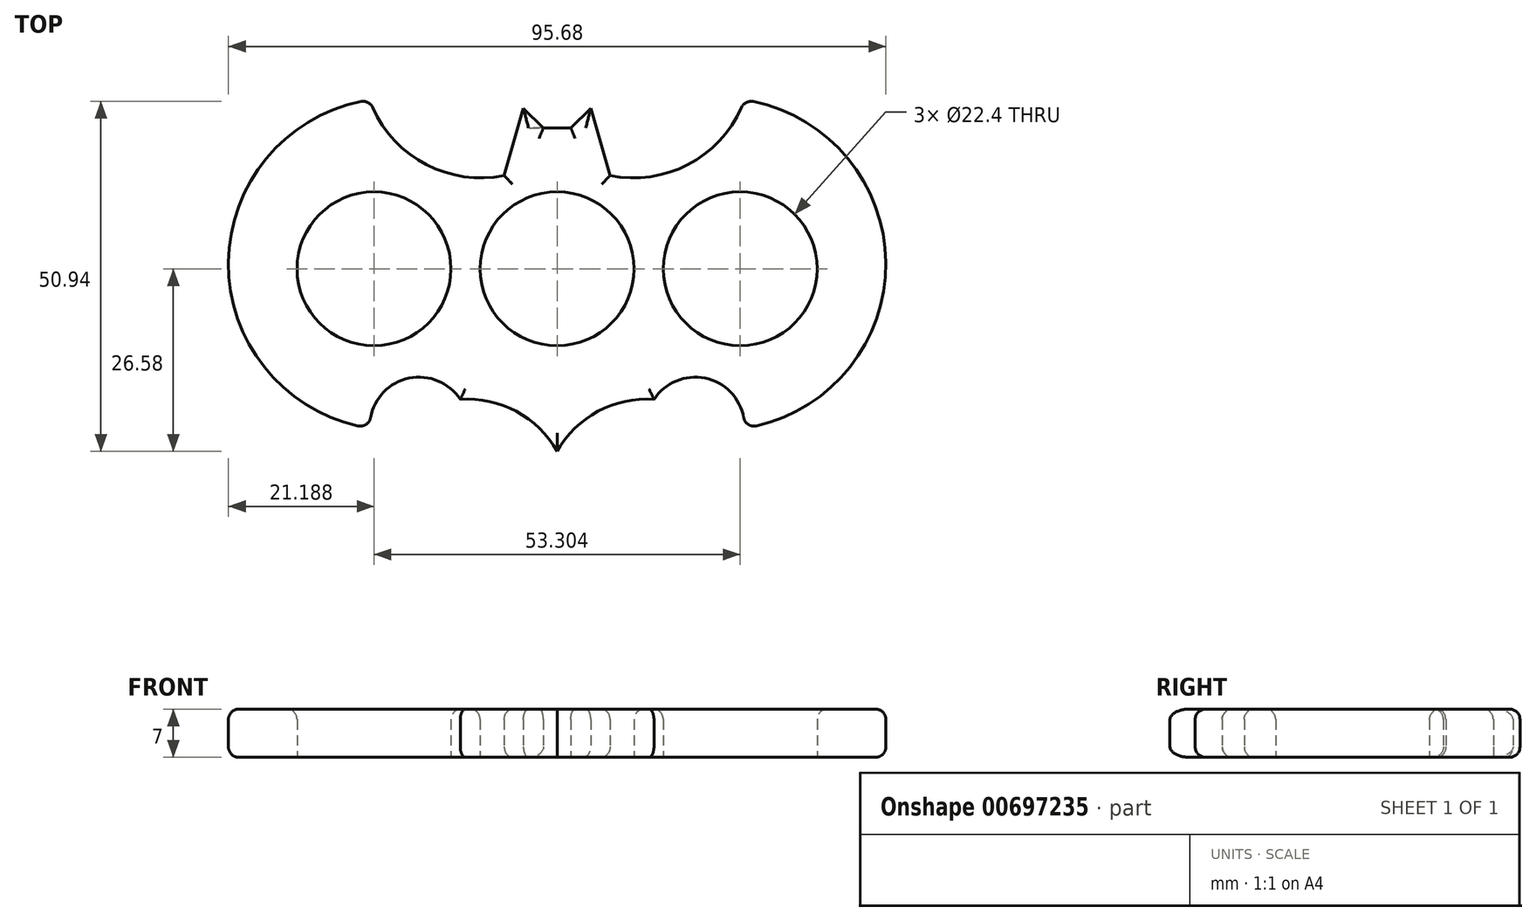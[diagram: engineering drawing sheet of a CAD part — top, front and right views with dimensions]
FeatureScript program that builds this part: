
annotation { "Feature Type Name" : "Feature", "Feature Type Description" : "" }
export const myFeature = defineFeature(function(context is Context, id is Id, definition is map)
    precondition{}
    {
        {
            var Q0;
            Q0=qCreatedBy(makeId("Top.planeOp"),FACE);
            var sketch = newSketch(context, id + "F0", { "sketchPlane" : qUnion([Q0])});
            skCircle(sketch, "E0", {"center": v(0, 0) * mm, "radius": 11.2 * mm});
            skCircle(sketch, "E1", {"center": v(26.65, 0) * mm, "radius": 11.2 * mm});
            skCircle(sketch, "E2.1.1", {"center": v(-26.65, 0) * mm, "radius": 11.2 * mm});
            skPoint(sketch, "E3.MirrorCS.end.orphan", {"position": v(7.9, 16.16) * mm});
            skPoint(sketch, "E4.end.orphan", {"position": v(-7.9, 16.16) * mm});
            skLineSegment(sketch, "E5", {"start": v(-7.7, 13.57) * mm, "end": v(-4.9, 23.35) * mm});
            skLineSegment(sketch, "E6", {"start": v(-4.9, 23.35) * mm, "end": v(-2, 20.49) * mm});
            skLineSegment(sketch, "E7.MirrorCS", {"start": v(7.7, 13.57) * mm, "end": v(4.9, 23.35) * mm});
            skLineSegment(sketch, "E8.MirrorCS", {"start": v(4.9, 23.35) * mm, "end": v(2, 20.49) * mm});
            skArc(sketch, "E9", {"start": v(-27.28, 24.55) * mm, "mid": v(-47.84, 0.68) * mm, "end": v(-27.28, -23.19) * mm});
            skPoint(sketch, "E10.MirrorCS.end.orphan", {"position": v(7.7, 13.57) * mm});
            skArc(sketch, "E11", {"start": v(-27.28, 24.55) * mm, "mid": v(-19.53, 15.43) * mm, "end": v(-7.7, 13.57) * mm});
            skLineSegment(sketch, "E12", {"start": v(-2, 20.49) * mm, "end": v(2, 20.49) * mm});
            skArc(sketch, "E13", {"start": v(-14.1, -19) * mm, "mid": v(-22.27, -16.11) * mm, "end": v(-27.28, -23.19) * mm});
            skArc(sketch, "E14", {"start": v(0, -26.58) * mm, "mid": v(-5.95, -20.75) * mm, "end": v(-14.1, -19) * mm});
            skArc(sketch, "E15.MirrorCS", {"start": v(27.28, 24.55) * mm, "mid": v(19.53, 15.43) * mm, "end": v(7.7, 13.57) * mm});
            skArc(sketch, "E16.MirrorCS", {"start": v(27.28, 24.55) * mm, "mid": v(47.84, 0.68) * mm, "end": v(27.28, -23.19) * mm});
            skArc(sketch, "E17.MirrorCS", {"start": v(14.1, -19) * mm, "mid": v(22.27, -16.11) * mm, "end": v(27.28, -23.19) * mm});
            skArc(sketch, "E18.MirrorCS", {"start": v(0, -26.58) * mm, "mid": v(5.95, -20.75) * mm, "end": v(14.1, -19) * mm});
            skSolve(sketch);
        }
        {
            var Q0;
            Q0=makeQuery(id+"F0.imprint","IMPRINT",FACE,{"disambiguationData":[TD([[makeQuery(id+"F0.imprint","IMPRINT",EDGE,{"derivedFrom":sQuery(id+"F0.wireOp",EDGE,"E0")}),-1.0]])]});
            extrude(context, id + "F1", {"entities" : qUnion([Q0]), "depth" : 7 * mm, "offsetDistance" : 25 * mm});
        }
        {
            var Q0;
            Q0=makeQuery(id+"F1.opExtrude","CAP_FACE",FACE,{"disambiguationData":[OSD([sQuery(id+"F0.wireOp",EDGE,"E0"),sQuery(id+"F0.wireOp",EDGE,"E1"),sQuery(id+"F0.wireOp",EDGE,"E2.1.1"),sQuery(id+"F0.wireOp",EDGE,"E5"),sQuery(id+"F0.wireOp",EDGE,"E6"),sQuery(id+"F0.wireOp",EDGE,"E8.MirrorCS"),sQuery(id+"F0.wireOp",EDGE,"E9"),sQuery(id+"F0.wireOp",EDGE,"E11"),sQuery(id+"F0.wireOp",EDGE,"E12"),sQuery(id+"F0.wireOp",EDGE,"E13"),sQuery(id+"F0.wireOp",EDGE,"E14"),sQuery(id+"F0.wireOp",EDGE,"E7.MirrorCS"),sQuery(id+"F0.wireOp",EDGE,"E15.MirrorCS"),sQuery(id+"F0.wireOp",EDGE,"E16.MirrorCS"),sQuery(id+"F0.wireOp",EDGE,"E17.MirrorCS"),sQuery(id+"F0.wireOp",EDGE,"E18.MirrorCS")])],"isStart":false});
            var Q1;
            Q1=makeQuery(id+"F1.opExtrude","SWEPT_FACE",FACE,{"disambiguationData":[OSD([sQuery(id+"F0.wireOp",EDGE,"E16.MirrorCS")])]});
            var Q2;
            Q2=makeQuery(id+"F1.opExtrude","SWEPT_FACE",FACE,{"disambiguationData":[OSD([sQuery(id+"F0.wireOp",EDGE,"E9")])]});
            var Q3;
            Q3=makeQuery(id+"F1.opExtrude","CAP_EDGE",EDGE,{"disambiguationData":[OSD([sQuery(id+"F0.wireOp",EDGE,"E18.MirrorCS")])],"isStart":true});
            var Q4;
            Q4=makeQuery(id+"F1.opExtrude","CAP_EDGE",EDGE,{"disambiguationData":[OSD([sQuery(id+"F0.wireOp",EDGE,"E17.MirrorCS")])],"isStart":true});
            var Q5;
            Q5=makeQuery(id+"F1.opExtrude","CAP_EDGE",EDGE,{"disambiguationData":[OSD([sQuery(id+"F0.wireOp",EDGE,"E14")])],"isStart":true});
            var Q6;
            Q6=makeQuery(id+"F1.opExtrude","CAP_EDGE",EDGE,{"disambiguationData":[OSD([sQuery(id+"F0.wireOp",EDGE,"E13")])],"isStart":true});
            var Q7;
            Q7=makeQuery(id+"F1.opExtrude","CAP_EDGE",EDGE,{"disambiguationData":[OSD([sQuery(id+"F0.wireOp",EDGE,"E15.MirrorCS")])],"isStart":true});
            var Q8;
            Q8=makeQuery(id+"F1.opExtrude","CAP_EDGE",EDGE,{"disambiguationData":[OSD([sQuery(id+"F0.wireOp",EDGE,"E6")])],"isStart":true});
            var Q9;
            Q9=makeQuery(id+"F1.opExtrude","CAP_EDGE",EDGE,{"disambiguationData":[OSD([sQuery(id+"F0.wireOp",EDGE,"E11")])],"isStart":true});
            var Q10;
            Q10=makeQuery(id+"F1.opExtrude","CAP_EDGE",EDGE,{"disambiguationData":[OSD([sQuery(id+"F0.wireOp",EDGE,"E5")])],"isStart":true});
            var Q11;
            Q11=makeQuery(id+"F1.opExtrude","CAP_EDGE",EDGE,{"disambiguationData":[OSD([sQuery(id+"F0.wireOp",EDGE,"E7.MirrorCS")])],"isStart":true});
            fillet(context, id + "F2", {"entities" : qUnion([Q0, Q1, Q2, Q3, Q4, Q5, Q6, Q7, Q8, Q9, Q10, Q11]), "radius" : 1.5 * mm, "tangentPropagation" : true, "allowEdgeOverflow" : false});
        }
    });
